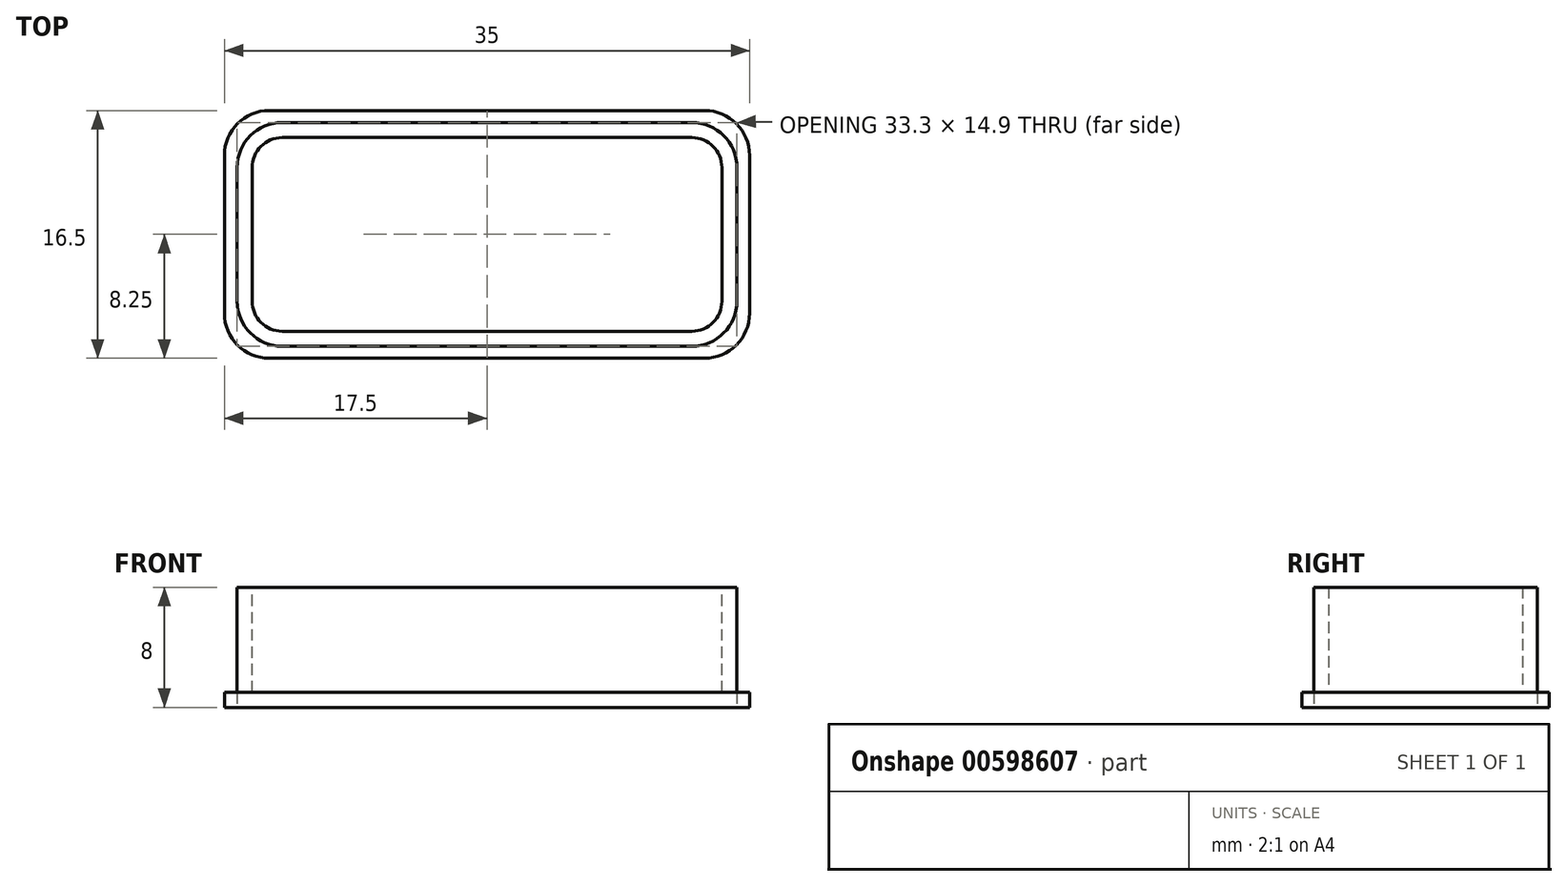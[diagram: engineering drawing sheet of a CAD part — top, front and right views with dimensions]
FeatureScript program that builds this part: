
annotation { "Feature Type Name" : "Feature", "Feature Type Description" : "" }
export const myFeature = defineFeature(function(context is Context, id is Id, definition is map)
    precondition{}
    {
        {
            var Q0;
            Q0=qCreatedBy(makeId("Top.planeOp"),FACE);
            var sketch = newSketch(context, id + "F0", { "sketchPlane" : qUnion([Q0])});
            skLineSegment(sketch, "E0.bottom", {"start": v(13.65, -7.45) * mm, "end": v(-13.65, -7.45) * mm});
            skLineSegment(sketch, "E0.top", {"start": v(13.65, 7.45) * mm, "end": v(-13.65, 7.45) * mm});
            skLineSegment(sketch, "E0.left", {"start": v(16.65, -4.45) * mm, "end": v(16.65, 4.45) * mm});
            skLineSegment(sketch, "E0.right", {"start": v(-16.65, -4.45) * mm, "end": v(-16.65, 4.45) * mm});
            skPoint(sketch, "E0.middle", {"position": v(0, 0) * mm});
            skPoint(sketch, "E1.visualSharp", {"position": v(16.65, 7.45) * mm});
            skArc(sketch, "E1.filletArc", {"start": v(16.65, 4.45) * mm, "mid": v(15.77, 6.57) * mm, "end": v(13.65, 7.45) * mm});
            skPoint(sketch, "E2.visualSharp", {"position": v(16.65, -7.45) * mm});
            skArc(sketch, "E2.filletArc", {"start": v(13.65, -7.45) * mm, "mid": v(15.77, -6.57) * mm, "end": v(16.65, -4.45) * mm});
            skPoint(sketch, "E3.visualSharp", {"position": v(-16.65, -7.45) * mm});
            skArc(sketch, "E3.filletArc", {"start": v(-16.65, -4.45) * mm, "mid": v(-15.77, -6.57) * mm, "end": v(-13.65, -7.45) * mm});
            skPoint(sketch, "E4.visualSharp", {"position": v(-16.65, 7.45) * mm});
            skArc(sketch, "E4.filletArc", {"start": v(-13.65, 7.45) * mm, "mid": v(-15.77, 6.57) * mm, "end": v(-16.65, 4.45) * mm});
            skSolve(sketch);
        }
        {
            var Q0;
            Q0=makeQuery(id+"F0.imprint","IMPRINT",FACE,{"disambiguationData":[TD([[makeQuery(id+"F0.imprint","IMPRINT",EDGE,{"derivedFrom":sQuery(id+"F0.wireOp",EDGE,"E0.bottom")}),-1.0]])]});
            extrude(context, id + "F1", {"entities" : qUnion([Q0]), "depth" : 8 * mm, "offsetDistance" : 25 * mm});
        }
        {
            var Q0;
            Q0=makeQuery(id+"F1.opExtrude","CAP_FACE",FACE,{"disambiguationData":[OSD([sQuery(id+"F0.wireOp",EDGE,"E0.bottom"),sQuery(id+"F0.wireOp",EDGE,"E0.top"),sQuery(id+"F0.wireOp",EDGE,"E0.left"),sQuery(id+"F0.wireOp",EDGE,"E0.right"),sQuery(id+"F0.wireOp",EDGE,"E1.filletArc"),sQuery(id+"F0.wireOp",EDGE,"E2.filletArc"),sQuery(id+"F0.wireOp",EDGE,"E3.filletArc"),sQuery(id+"F0.wireOp",EDGE,"E4.filletArc")])],"isStart":false});
            shell(context, id + "F2", {"entities" : qUnion([Q0]), "thickness" : 1 * mm});
        }
        {
            var Q0;
            Q0=makeQuery(id+"F1.opExtrude","CAP_FACE",FACE,{"disambiguationData":[OSD([sQuery(id+"F0.wireOp",EDGE,"E0.bottom"),sQuery(id+"F0.wireOp",EDGE,"E0.top"),sQuery(id+"F0.wireOp",EDGE,"E0.left"),sQuery(id+"F0.wireOp",EDGE,"E0.right"),sQuery(id+"F0.wireOp",EDGE,"E1.filletArc"),sQuery(id+"F0.wireOp",EDGE,"E2.filletArc"),sQuery(id+"F0.wireOp",EDGE,"E3.filletArc"),sQuery(id+"F0.wireOp",EDGE,"E4.filletArc")])],"isStart":true});
            var sketch = newSketch(context, id + "F3", { "sketchPlane" : qUnion([Q0])});
            skLineSegment(sketch, "E5.bottom", {"start": v(14.5, -8.25) * mm, "end": v(-14.5, -8.25) * mm});
            skLineSegment(sketch, "E5.top", {"start": v(14.5, 8.25) * mm, "end": v(-14.5, 8.25) * mm});
            skLineSegment(sketch, "E5.left", {"start": v(17.5, -5.25) * mm, "end": v(17.5, 5.25) * mm});
            skLineSegment(sketch, "E5.right", {"start": v(-17.5, -5.25) * mm, "end": v(-17.5, 5.25) * mm});
            skPoint(sketch, "E5.middle", {"position": v(0, 0) * mm});
            skPoint(sketch, "E6.visualSharp", {"position": v(17.5, 8.25) * mm});
            skArc(sketch, "E6.filletArc", {"start": v(17.5, 5.25) * mm, "mid": v(16.62, 7.37) * mm, "end": v(14.5, 8.25) * mm});
            skPoint(sketch, "E7.visualSharp", {"position": v(17.5, -8.25) * mm});
            skArc(sketch, "E7.filletArc", {"start": v(14.5, -8.25) * mm, "mid": v(16.62, -7.37) * mm, "end": v(17.5, -5.25) * mm});
            skPoint(sketch, "E8.visualSharp", {"position": v(-17.5, -8.25) * mm});
            skArc(sketch, "E8.filletArc", {"start": v(-17.5, -5.25) * mm, "mid": v(-16.62, -7.37) * mm, "end": v(-14.5, -8.25) * mm});
            skPoint(sketch, "E9.visualSharp", {"position": v(-17.5, 8.25) * mm});
            skArc(sketch, "E9.filletArc", {"start": v(-14.5, 8.25) * mm, "mid": v(-16.62, 7.37) * mm, "end": v(-17.5, 5.25) * mm});
            skSolve(sketch);
        }
        {
            var Q0;
            Q0=makeQuery(id+"F3.imprint","IMPRINT",FACE,{"disambiguationData":[TD([[makeQuery(id+"F3.imprint","IMPRINT",EDGE,{"derivedFrom":sQuery(id+"F3.wireOp",EDGE,"E5.bottom")}),-1.0]])]});
            extrude(context, id + "F4", {"entities" : qUnion([Q0]), "oppositeDirection" : true, "depth" : 1 * mm, "offsetDistance" : 25 * mm});
        }
    });
